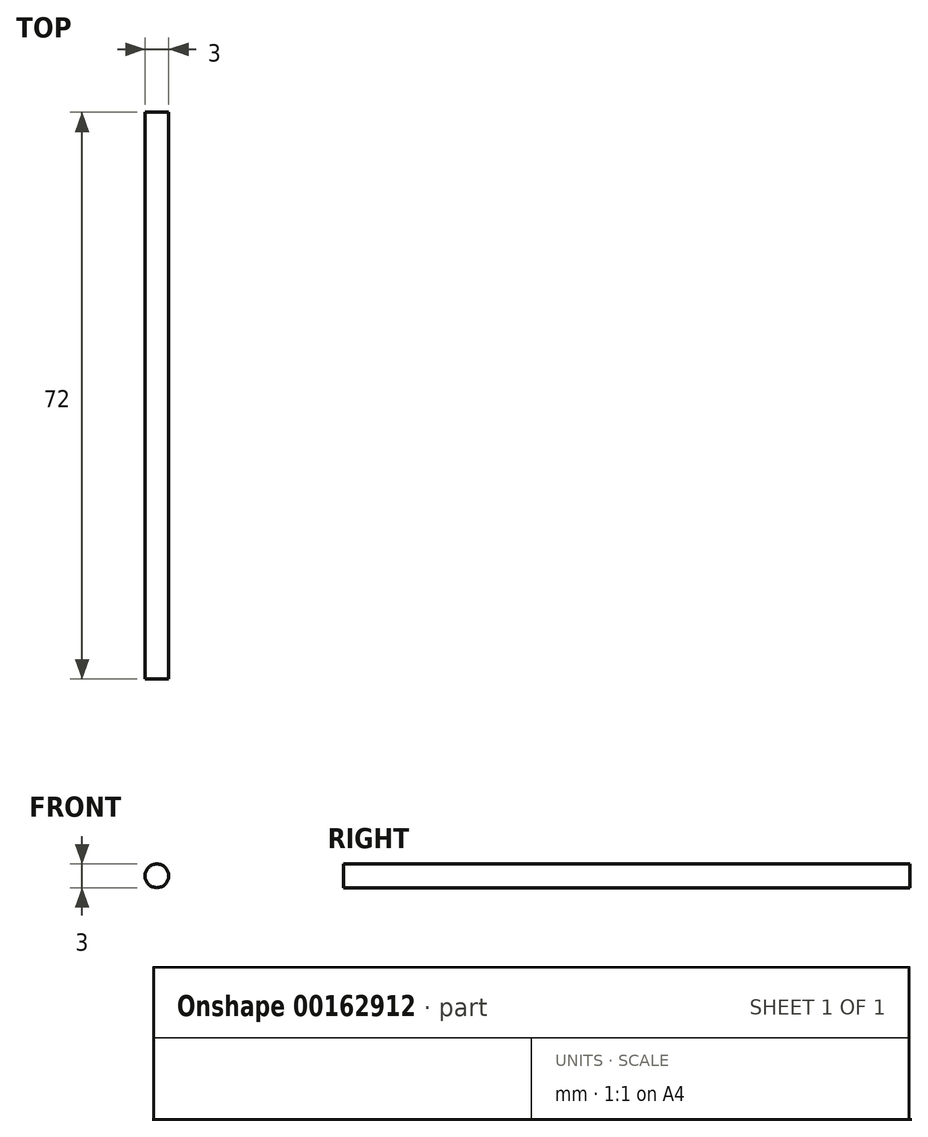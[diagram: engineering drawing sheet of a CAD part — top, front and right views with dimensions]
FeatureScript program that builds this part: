
annotation { "Feature Type Name" : "Feature", "Feature Type Description" : "" }
export const myFeature = defineFeature(function(context is Context, id is Id, definition is map)
    precondition{}
    {
        {
            var Q0;
            Q0=qCreatedBy(makeId("Front.planeOp"),FACE);
            var sketch = newSketch(context, id + "F0", { "sketchPlane" : qUnion([Q0])});
            skCircle(sketch, "E0", {"center": v(0, 0) * mm, "radius": 1.5 * mm});
            skSolve(sketch);
        }
        {
            var Q0;
            Q0=makeQuery(id+"F0.imprint","IMPRINT",FACE,{"disambiguationData":[TD([[makeQuery(id+"F0.imprint","IMPRINT",EDGE,{"derivedFrom":sQuery(id+"F0.wireOp",EDGE,"E0")}),1.0]])]});
            extrude(context, id + "F1", {"entities" : qUnion([Q0]), "depth" : 72 * mm});
        }
    });
